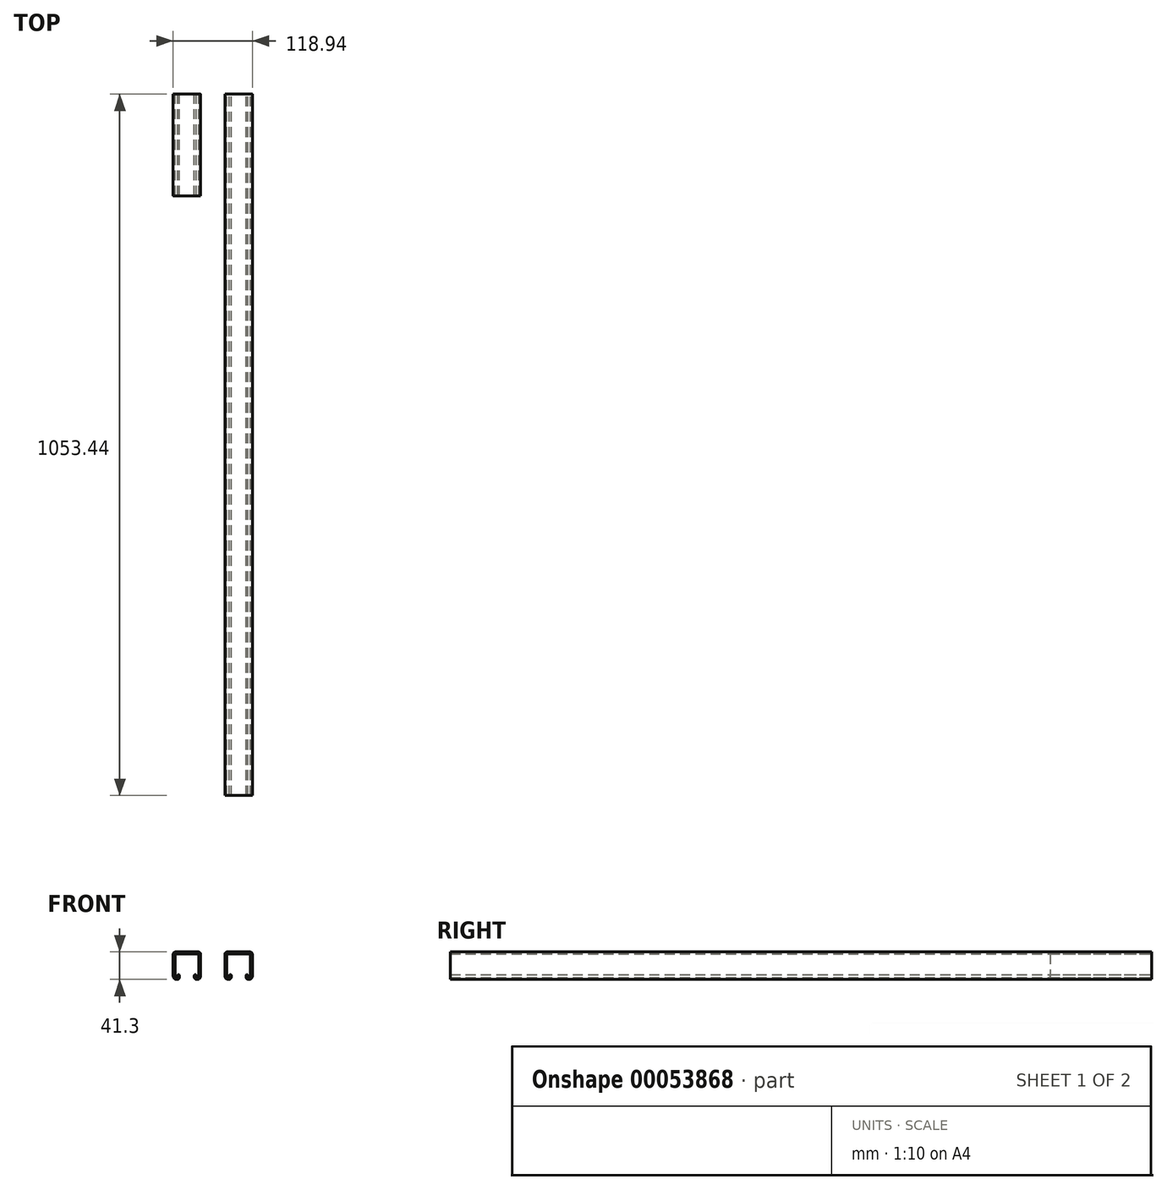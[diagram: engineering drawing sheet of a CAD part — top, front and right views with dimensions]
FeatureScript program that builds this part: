
annotation { "Feature Type Name" : "Feature", "Feature Type Description" : "" }
export const myFeature = defineFeature(function(context is Context, id is Id, definition is map)
    precondition{}
    {
        {
            var Q0;
            Q0=qCreatedBy(makeId("Front.planeOp"),FACE);
            var sketch = newSketch(context, id + "F0", { "sketchPlane" : qUnion([Q0])});
            skArc(sketch, "E0.0", {"start": v(5.05, 41.29) * mm, "mid": v(1.47, 39.8) * mm, "end": v(-0.01, 36.23) * mm});
            skFitSpline(sketch, "E0.1", {"points": [v(6.06, 41.29) * mm, v(5.73, 41.29) * mm, v(5.39, 41.29) * mm, v(5.05, 41.29) * mm]});
            skArc(sketch, "E0.2", {"start": v(9.54, 37.81) * mm, "mid": v(8.52, 40.27) * mm, "end": v(6.06, 41.29) * mm});
            skFitSpline(sketch, "E0.3", {"points": [v(9.54, 35.47) * mm, v(9.54, 36.25) * mm, v(9.54, 37.03) * mm, v(9.54, 37.81) * mm]});
            skArc(sketch, "E0.4", {"start": v(6.85, 35.47) * mm, "mid": v(8.2, 34.13) * mm, "end": v(9.54, 35.47) * mm});
            skFitSpline(sketch, "E0.5", {"points": [v(34.43, 35.47) * mm, v(34.43, 36.25) * mm, v(34.43, 37.03) * mm, v(34.43, 37.81) * mm]});
            skArc(sketch, "E0.6", {"start": v(31.74, 35.47) * mm, "mid": v(33.08, 34.13) * mm, "end": v(34.43, 35.47) * mm});
            skFitSpline(sketch, "E0.7", {"points": [v(31.74, 37.81) * mm, v(31.74, 37.03) * mm, v(31.74, 36.25) * mm, v(31.74, 35.47) * mm]});
            skArc(sketch, "E0.8", {"start": v(35.21, 41.29) * mm, "mid": v(32.75, 40.27) * mm, "end": v(31.74, 37.81) * mm});
            skFitSpline(sketch, "E0.9", {"points": [v(36.23, 41.29) * mm, v(35.89, 41.29) * mm, v(35.55, 41.29) * mm, v(35.21, 41.29) * mm]});
            skArc(sketch, "E0.10", {"start": v(41.29, 36.23) * mm, "mid": v(39.8, 39.8) * mm, "end": v(36.23, 41.29) * mm});
            skArc(sketch, "E0.11", {"start": v(-0.01, 3.46) * mm, "mid": v(1, 1) * mm, "end": v(3.46, -0.01) * mm});
            skFitSpline(sketch, "E0.12", {"points": [v(3.46, -0.01) * mm, v(14.91, -0.01) * mm, v(26.36, -0.01) * mm, v(37.81, -0.01) * mm]});
            skArc(sketch, "E0.13", {"start": v(37.81, -0.01) * mm, "mid": v(40.27, 1) * mm, "end": v(41.29, 3.46) * mm});
            skFitSpline(sketch, "E0.14", {"points": [v(41.29, 3.46) * mm, v(41.29, 14.38) * mm, v(41.29, 25.3) * mm, v(41.29, 36.23) * mm]});
            skArc(sketch, "E0.15", {"start": v(34.43, 37.81) * mm, "mid": v(34.66, 38.37) * mm, "end": v(35.21, 38.6) * mm});
            skFitSpline(sketch, "E0.16", {"points": [v(35.21, 38.6) * mm, v(35.55, 38.6) * mm, v(35.89, 38.6) * mm, v(36.23, 38.6) * mm]});
            skArc(sketch, "E0.17", {"start": v(36.23, 38.6) * mm, "mid": v(37.9, 37.9) * mm, "end": v(38.6, 36.23) * mm});
            skFitSpline(sketch, "E0.18", {"points": [v(38.6, 3.46) * mm, v(38.6, 14.38) * mm, v(38.6, 25.3) * mm, v(38.6, 36.23) * mm]});
            skArc(sketch, "E0.19", {"start": v(38.6, 3.46) * mm, "mid": v(38.37, 2.9) * mm, "end": v(37.81, 2.68) * mm});
            skFitSpline(sketch, "E0.20", {"points": [v(-0.01, 36.23) * mm, v(-0.01, 25.3) * mm, v(-0.01, 14.38) * mm, v(-0.01, 3.46) * mm]});
            skFitSpline(sketch, "E0.21", {"points": [v(37.81, 2.68) * mm, v(26.36, 2.68) * mm, v(14.91, 2.68) * mm, v(3.46, 2.68) * mm]});
            skArc(sketch, "E0.22", {"start": v(3.46, 2.68) * mm, "mid": v(2.9, 2.9) * mm, "end": v(2.68, 3.46) * mm});
            skFitSpline(sketch, "E0.23", {"points": [v(2.68, 3.46) * mm, v(2.68, 14.38) * mm, v(2.68, 25.3) * mm, v(2.68, 36.23) * mm]});
            skArc(sketch, "E0.24", {"start": v(2.68, 36.23) * mm, "mid": v(3.37, 37.9) * mm, "end": v(5.05, 38.6) * mm});
            skFitSpline(sketch, "E0.25", {"points": [v(5.05, 38.6) * mm, v(5.39, 38.6) * mm, v(5.73, 38.6) * mm, v(6.06, 38.6) * mm]});
            skArc(sketch, "E0.26", {"start": v(6.06, 38.6) * mm, "mid": v(6.62, 38.37) * mm, "end": v(6.85, 37.81) * mm});
            skFitSpline(sketch, "E0.27", {"points": [v(6.85, 37.81) * mm, v(6.85, 37.03) * mm, v(6.85, 36.25) * mm, v(6.85, 35.47) * mm]});
            skLineSegment(sketch, "E1", {"start": v(-9.67, -3.97) * mm, "end": v(55.26, -3.97) * mm});
            skFitSpline(sketch, "E2.MirrorCS", {"points": [v(-0.01, -44.16) * mm, v(-0.01, -33.24) * mm, v(-0.01, -22.32) * mm, v(-0.01, -11.4) * mm]});
            skFitSpline(sketch, "E3.MirrorCS", {"points": [v(2.68, -11.4) * mm, v(2.68, -22.32) * mm, v(2.68, -33.24) * mm, v(2.68, -44.16) * mm]});
            skArc(sketch, "E4.MirrorCS", {"start": v(5.05, -49.22) * mm, "mid": v(1.47, -47.74) * mm, "end": v(-0.01, -44.16) * mm});
            skArc(sketch, "E5.MirrorCS", {"start": v(9.54, -45.75) * mm, "mid": v(8.52, -48.2) * mm, "end": v(6.06, -49.22) * mm});
            skFitSpline(sketch, "E6.MirrorCS", {"points": [v(9.54, -43.4) * mm, v(9.54, -44.19) * mm, v(9.54, -44.97) * mm, v(9.54, -45.75) * mm]});
            skArc(sketch, "E7.MirrorCS", {"start": v(6.85, -43.4) * mm, "mid": v(8.2, -42.06) * mm, "end": v(9.54, -43.4) * mm});
            skFitSpline(sketch, "E8.MirrorCS", {"points": [v(6.85, -45.75) * mm, v(6.85, -44.97) * mm, v(6.85, -44.19) * mm, v(6.85, -43.4) * mm]});
            skArc(sketch, "E9.MirrorCS", {"start": v(6.06, -46.53) * mm, "mid": v(6.62, -46.3) * mm, "end": v(6.85, -45.75) * mm});
            skFitSpline(sketch, "E10.MirrorCS", {"points": [v(5.05, -46.53) * mm, v(5.39, -46.53) * mm, v(5.73, -46.53) * mm, v(6.06, -46.53) * mm]});
            skArc(sketch, "E11.MirrorCS", {"start": v(2.68, -44.16) * mm, "mid": v(3.37, -45.84) * mm, "end": v(5.05, -46.53) * mm});
            skFitSpline(sketch, "E12.MirrorCS", {"points": [v(6.06, -49.22) * mm, v(5.73, -49.22) * mm, v(5.39, -49.22) * mm, v(5.05, -49.22) * mm]});
            skArc(sketch, "E13.MirrorCS", {"start": v(3.46, -10.61) * mm, "mid": v(2.9, -10.84) * mm, "end": v(2.68, -11.4) * mm});
            skArc(sketch, "E14.MirrorCS", {"start": v(-0.01, -11.4) * mm, "mid": v(1, -8.94) * mm, "end": v(3.46, -7.92) * mm});
            skFitSpline(sketch, "E15.MirrorCS", {"points": [v(3.46, -7.92) * mm, v(14.91, -7.92) * mm, v(26.36, -7.92) * mm, v(37.81, -7.92) * mm]});
            skFitSpline(sketch, "E16.MirrorCS", {"points": [v(37.81, -10.61) * mm, v(26.36, -10.61) * mm, v(14.91, -10.61) * mm, v(3.46, -10.61) * mm]});
            skArc(sketch, "E17.MirrorCS", {"start": v(37.81, -7.92) * mm, "mid": v(40.27, -8.94) * mm, "end": v(41.29, -11.4) * mm});
            skFitSpline(sketch, "E18.MirrorCS", {"points": [v(38.6, -11.4) * mm, v(38.6, -22.32) * mm, v(38.6, -33.24) * mm, v(38.6, -44.16) * mm]});
            skFitSpline(sketch, "E19.MirrorCS", {"points": [v(41.29, -11.4) * mm, v(41.29, -22.32) * mm, v(41.29, -33.24) * mm, v(41.29, -44.16) * mm]});
            skArc(sketch, "E20.MirrorCS", {"start": v(38.6, -11.4) * mm, "mid": v(38.37, -10.84) * mm, "end": v(37.81, -10.61) * mm});
            skArc(sketch, "E21.MirrorCS", {"start": v(31.74, -43.4) * mm, "mid": v(33.08, -42.06) * mm, "end": v(34.43, -43.4) * mm});
            skFitSpline(sketch, "E22.MirrorCS", {"points": [v(31.74, -45.75) * mm, v(31.74, -44.97) * mm, v(31.74, -44.19) * mm, v(31.74, -43.4) * mm]});
            skArc(sketch, "E23.MirrorCS", {"start": v(35.21, -49.22) * mm, "mid": v(32.75, -48.2) * mm, "end": v(31.74, -45.75) * mm});
            skFitSpline(sketch, "E24.MirrorCS", {"points": [v(36.23, -49.22) * mm, v(35.89, -49.22) * mm, v(35.55, -49.22) * mm, v(35.21, -49.22) * mm]});
            skArc(sketch, "E25.MirrorCS", {"start": v(34.43, -45.75) * mm, "mid": v(34.66, -46.3) * mm, "end": v(35.21, -46.53) * mm});
            skFitSpline(sketch, "E26.MirrorCS", {"points": [v(34.43, -43.4) * mm, v(34.43, -44.19) * mm, v(34.43, -44.97) * mm, v(34.43, -45.75) * mm]});
            skFitSpline(sketch, "E27.MirrorCS", {"points": [v(35.21, -46.53) * mm, v(35.55, -46.53) * mm, v(35.89, -46.53) * mm, v(36.23, -46.53) * mm]});
            skArc(sketch, "E28.MirrorCS", {"start": v(36.23, -46.53) * mm, "mid": v(37.9, -45.84) * mm, "end": v(38.6, -44.16) * mm});
            skArc(sketch, "E29.MirrorCS", {"start": v(41.29, -44.16) * mm, "mid": v(39.8, -47.74) * mm, "end": v(36.23, -49.22) * mm});
            skLineSegment(sketch, "E30", {"start": v(63.23, 49.88) * mm, "end": v(63.23, -3.52) * mm});
            skFitSpline(sketch, "E31.MirrorCS", {"points": [v(85.18, 3.46) * mm, v(85.18, 14.38) * mm, v(85.18, 25.3) * mm, v(85.18, 36.23) * mm]});
            skFitSpline(sketch, "E32.MirrorCS", {"points": [v(87.87, 3.46) * mm, v(87.87, 14.38) * mm, v(87.87, 25.3) * mm, v(87.87, 36.23) * mm]});
            skFitSpline(sketch, "E33.MirrorCS", {"points": [v(123.79, 3.46) * mm, v(123.79, 14.38) * mm, v(123.79, 25.3) * mm, v(123.79, 36.23) * mm]});
            skFitSpline(sketch, "E34.MirrorCS", {"points": [v(126.48, 36.23) * mm, v(126.48, 25.3) * mm, v(126.48, 14.38) * mm, v(126.48, 3.46) * mm]});
            skArc(sketch, "E35.MirrorCS", {"start": v(126.48, 3.46) * mm, "mid": v(125.46, 1) * mm, "end": v(123, -0.01) * mm});
            skFitSpline(sketch, "E36.MirrorCS", {"points": [v(88.65, 2.68) * mm, v(100.1, 2.68) * mm, v(111.56, 2.68) * mm, v(123, 2.68) * mm]});
            skFitSpline(sketch, "E37.MirrorCS", {"points": [v(123, -0.01) * mm, v(111.56, -0.01) * mm, v(100.1, -0.01) * mm, v(88.65, -0.01) * mm]});
            skArc(sketch, "E38.MirrorCS", {"start": v(88.65, -0.01) * mm, "mid": v(86.2, 1) * mm, "end": v(85.18, 3.46) * mm});
            skFitSpline(sketch, "E39.MirrorCS", {"points": [v(85.18, 3.46) * mm, v(85.18, 14.38) * mm, v(85.18, 25.3) * mm, v(85.18, 36.23) * mm]});
            skArc(sketch, "E40.MirrorCS", {"start": v(90.24, 38.6) * mm, "mid": v(88.57, 37.9) * mm, "end": v(87.87, 36.23) * mm});
            skArc(sketch, "E41.MirrorCS", {"start": v(85.18, 36.23) * mm, "mid": v(86.66, 39.8) * mm, "end": v(90.24, 41.29) * mm});
            skFitSpline(sketch, "E42.MirrorCS", {"points": [v(90.24, 41.29) * mm, v(90.58, 41.29) * mm, v(90.92, 41.29) * mm, v(91.26, 41.29) * mm]});
            skArc(sketch, "E43.MirrorCS", {"start": v(91.26, 41.29) * mm, "mid": v(93.71, 40.27) * mm, "end": v(94.73, 37.81) * mm});
            skFitSpline(sketch, "E44.MirrorCS", {"points": [v(94.73, 37.81) * mm, v(94.73, 37.03) * mm, v(94.73, 36.25) * mm, v(94.73, 35.47) * mm]});
            skArc(sketch, "E45.MirrorCS", {"start": v(94.73, 35.47) * mm, "mid": v(93.39, 34.13) * mm, "end": v(92.04, 35.47) * mm});
            skFitSpline(sketch, "E46.MirrorCS", {"points": [v(92.04, 35.47) * mm, v(92.04, 36.25) * mm, v(92.04, 37.03) * mm, v(92.04, 37.81) * mm]});
            skArc(sketch, "E47.MirrorCS", {"start": v(92.04, 37.81) * mm, "mid": v(91.81, 38.37) * mm, "end": v(91.26, 38.6) * mm});
            skArc(sketch, "E48.MirrorCS", {"start": v(121.42, 41.29) * mm, "mid": v(125, 39.8) * mm, "end": v(126.48, 36.23) * mm});
            skFitSpline(sketch, "E49.MirrorCS", {"points": [v(120.4, 41.29) * mm, v(120.74, 41.29) * mm, v(121.08, 41.29) * mm, v(121.42, 41.29) * mm]});
            skArc(sketch, "E50.MirrorCS", {"start": v(123.79, 36.23) * mm, "mid": v(123.1, 37.9) * mm, "end": v(121.42, 38.6) * mm});
            skArc(sketch, "E51.MirrorCS", {"start": v(120.4, 38.6) * mm, "mid": v(119.85, 38.37) * mm, "end": v(119.62, 37.81) * mm});
            skFitSpline(sketch, "E52.MirrorCS", {"points": [v(119.62, 37.81) * mm, v(119.62, 37.03) * mm, v(119.62, 36.25) * mm, v(119.62, 35.47) * mm]});
            skArc(sketch, "E53.MirrorCS", {"start": v(119.62, 35.47) * mm, "mid": v(118.28, 34.13) * mm, "end": v(116.93, 35.47) * mm});
            skFitSpline(sketch, "E54.MirrorCS", {"points": [v(116.93, 35.47) * mm, v(116.93, 36.25) * mm, v(116.93, 37.03) * mm, v(116.93, 37.81) * mm]});
            skArc(sketch, "E55.MirrorCS", {"start": v(116.93, 37.81) * mm, "mid": v(117.95, 40.27) * mm, "end": v(120.4, 41.29) * mm});
            skArc(sketch, "E56.MirrorCS", {"start": v(87.87, 3.46) * mm, "mid": v(88.1, 2.9) * mm, "end": v(88.65, 2.68) * mm});
            skArc(sketch, "E57.MirrorCS", {"start": v(123, 2.68) * mm, "mid": v(123.56, 2.9) * mm, "end": v(123.79, 3.46) * mm});
            skFitSpline(sketch, "E58.MirrorCS", {"points": [v(91.26, 38.6) * mm, v(90.92, 38.6) * mm, v(90.58, 38.6) * mm, v(90.24, 38.6) * mm]});
            skFitSpline(sketch, "E59.MirrorCS", {"points": [v(121.42, 38.6) * mm, v(121.08, 38.6) * mm, v(120.74, 38.6) * mm, v(120.4, 38.6) * mm]});
            skArc(sketch, "E60.MirrorCS", {"start": v(88.65, 0.2) * mm, "mid": v(86.2, -0.8) * mm, "end": v(85.17, -3.26) * mm});
            skFitSpline(sketch, "E61.MirrorCS", {"points": [v(85.17, -3.26) * mm, v(85.12, -14.18) * mm, v(85.07, -25.1) * mm, v(85.02, -36.03) * mm]});
            skFitSpline(sketch, "E62.MirrorCS", {"points": [v(87.86, -3.27) * mm, v(87.8, -14.2) * mm, v(87.76, -25.12) * mm, v(87.7, -36.04) * mm]});
            skArc(sketch, "E63.MirrorCS", {"start": v(87.86, -3.27) * mm, "mid": v(88.09, -2.72) * mm, "end": v(88.64, -2.5) * mm});
            skFitSpline(sketch, "E64.MirrorCS", {"points": [v(88.64, -2.5) * mm, v(100.1, -2.55) * mm, v(111.54, -2.6) * mm, v(123, -2.65) * mm]});
            skArc(sketch, "E65.MirrorCS", {"start": v(123, -2.65) * mm, "mid": v(123.55, -2.88) * mm, "end": v(123.77, -3.43) * mm});
            skArc(sketch, "E66.MirrorCS", {"start": v(126.47, -3.45) * mm, "mid": v(125.46, -0.99) * mm, "end": v(123, 0.04) * mm});
            skFitSpline(sketch, "E67.MirrorCS", {"points": [v(126.32, -36.21) * mm, v(126.37, -25.3) * mm, v(126.42, -14.37) * mm, v(126.47, -3.45) * mm]});
            skFitSpline(sketch, "E68.MirrorCS", {"points": [v(123.77, -3.43) * mm, v(123.72, -14.36) * mm, v(123.68, -25.28) * mm, v(123.63, -36.2) * mm]});
            skArc(sketch, "E69.MirrorCS", {"start": v(85.02, -36.03) * mm, "mid": v(86.48, -39.61) * mm, "end": v(90.06, -41.1) * mm});
            skArc(sketch, "E70.MirrorCS", {"start": v(90.07, -38.42) * mm, "mid": v(88.4, -37.72) * mm, "end": v(87.7, -36.04) * mm});
            skFitSpline(sketch, "E71.MirrorCS", {"points": [v(90.06, -41.1) * mm, v(90.4, -41.11) * mm, v(90.73, -41.11) * mm, v(91.07, -41.11) * mm]});
            skFitSpline(sketch, "E72.MirrorCS", {"points": [v(91.08, -38.42) * mm, v(90.75, -38.42) * mm, v(90.4, -38.42) * mm, v(90.07, -38.42) * mm]});
            skArc(sketch, "E73.MirrorCS", {"start": v(91.87, -37.64) * mm, "mid": v(91.64, -38.2) * mm, "end": v(91.08, -38.42) * mm});
            skArc(sketch, "E74.MirrorCS", {"start": v(91.07, -41.11) * mm, "mid": v(93.53, -40.1) * mm, "end": v(94.56, -37.66) * mm});
            skFitSpline(sketch, "E75.MirrorCS", {"points": [v(94.56, -37.66) * mm, v(94.56, -36.88) * mm, v(94.57, -36.1) * mm, v(94.57, -35.31) * mm]});
            skArc(sketch, "E76.MirrorCS", {"start": v(94.57, -35.31) * mm, "mid": v(93.23, -33.96) * mm, "end": v(91.88, -35.3) * mm});
            skFitSpline(sketch, "E77.MirrorCS", {"points": [v(91.88, -35.3) * mm, v(91.88, -36.08) * mm, v(91.87, -36.86) * mm, v(91.87, -37.64) * mm]});
            skFitSpline(sketch, "E78.MirrorCS", {"points": [v(119.45, -37.77) * mm, v(119.46, -36.99) * mm, v(119.46, -36.2) * mm, v(119.46, -35.43) * mm]});
            skArc(sketch, "E79.MirrorCS", {"start": v(120.23, -38.55) * mm, "mid": v(119.68, -38.32) * mm, "end": v(119.45, -37.77) * mm});
            skFitSpline(sketch, "E80.MirrorCS", {"points": [v(121.25, -38.56) * mm, v(120.9, -38.56) * mm, v(120.57, -38.56) * mm, v(120.23, -38.55) * mm]});
            skArc(sketch, "E81.MirrorCS", {"start": v(123.63, -36.2) * mm, "mid": v(122.92, -37.87) * mm, "end": v(121.25, -38.56) * mm});
            skFitSpline(sketch, "E82.MirrorCS", {"points": [v(119.45, -37.77) * mm, v(119.46, -36.99) * mm, v(119.46, -36.2) * mm, v(119.46, -35.43) * mm]});
            skArc(sketch, "E83.MirrorCS", {"start": v(119.46, -35.43) * mm, "mid": v(118.12, -34.07) * mm, "end": v(116.77, -35.41) * mm});
            skFitSpline(sketch, "E84.MirrorCS", {"points": [v(116.77, -35.41) * mm, v(116.77, -36.2) * mm, v(116.76, -36.98) * mm, v(116.76, -37.76) * mm]});
            skArc(sketch, "E85.MirrorCS", {"start": v(116.76, -37.76) * mm, "mid": v(117.77, -40.22) * mm, "end": v(120.22, -41.25) * mm});
            skFitSpline(sketch, "E86.MirrorCS", {"points": [v(120.22, -41.25) * mm, v(120.56, -41.25) * mm, v(120.9, -41.25) * mm, v(121.23, -41.25) * mm]});
            skArc(sketch, "E87.MirrorCS", {"start": v(121.23, -41.25) * mm, "mid": v(124.82, -39.78) * mm, "end": v(126.32, -36.21) * mm});
            skFitSpline(sketch, "E88.MirrorCS", {"points": [v(126.32, -36.21) * mm, v(126.37, -25.3) * mm, v(126.42, -14.37) * mm, v(126.47, -3.45) * mm]});
            skLineSegment(sketch, "E89", {"start": v(-18.18, 60.45) * mm, "end": v(-18.18, -59.78) * mm});
            skFitSpline(sketch, "E90.MirrorCS", {"points": [v(-36.35, -44.16) * mm, v(-36.35, -33.24) * mm, v(-36.35, -22.32) * mm, v(-36.35, -11.4) * mm]});
            skFitSpline(sketch, "E91.MirrorCS", {"points": [v(-39.05, -11.4) * mm, v(-39.05, -22.32) * mm, v(-39.05, -33.24) * mm, v(-39.05, -44.16) * mm]});
            skArc(sketch, "E92.MirrorCS", {"start": v(-36.35, -11.4) * mm, "mid": v(-37.37, -8.94) * mm, "end": v(-39.83, -7.92) * mm});
            skArc(sketch, "E93.MirrorCS", {"start": v(-39.83, -10.61) * mm, "mid": v(-39.27, -10.84) * mm, "end": v(-39.05, -11.4) * mm});
            skFitSpline(sketch, "E94.MirrorCS", {"points": [v(-39.83, -7.92) * mm, v(-51.28, -7.92) * mm, v(-62.73, -7.92) * mm, v(-74.18, -7.92) * mm]});
            skFitSpline(sketch, "E95.MirrorCS", {"points": [v(-74.18, -10.61) * mm, v(-62.73, -10.61) * mm, v(-51.28, -10.61) * mm, v(-39.83, -10.61) * mm]});
            skArc(sketch, "E96.MirrorCS", {"start": v(-74.18, -7.92) * mm, "mid": v(-76.64, -8.94) * mm, "end": v(-77.65, -11.4) * mm});
            skFitSpline(sketch, "E97.MirrorCS", {"points": [v(-77.65, -11.4) * mm, v(-77.65, -22.32) * mm, v(-77.65, -33.24) * mm, v(-77.65, -44.16) * mm]});
            skArc(sketch, "E98.MirrorCS", {"start": v(-74.96, -11.4) * mm, "mid": v(-74.73, -10.84) * mm, "end": v(-74.18, -10.61) * mm});
            skFitSpline(sketch, "E99.MirrorCS", {"points": [v(-74.96, -11.4) * mm, v(-74.96, -22.32) * mm, v(-74.96, -33.24) * mm, v(-74.96, -44.16) * mm]});
            skArc(sketch, "E100.MirrorCS", {"start": v(-72.6, -46.53) * mm, "mid": v(-74.27, -45.84) * mm, "end": v(-74.96, -44.16) * mm});
            skArc(sketch, "E101.MirrorCS", {"start": v(-77.65, -44.16) * mm, "mid": v(-76.17, -47.74) * mm, "end": v(-72.6, -49.22) * mm});
            skFitSpline(sketch, "E102.MirrorCS", {"points": [v(-72.6, -49.22) * mm, v(-72.25, -49.22) * mm, v(-71.92, -49.22) * mm, v(-71.58, -49.22) * mm]});
            skFitSpline(sketch, "E103.MirrorCS", {"points": [v(-71.58, -46.53) * mm, v(-71.92, -46.53) * mm, v(-72.25, -46.53) * mm, v(-72.6, -46.53) * mm]});
            skArc(sketch, "E104.MirrorCS", {"start": v(-70.8, -45.75) * mm, "mid": v(-71.02, -46.3) * mm, "end": v(-71.58, -46.53) * mm});
            skFitSpline(sketch, "E105.MirrorCS", {"points": [v(-70.8, -43.4) * mm, v(-70.8, -44.19) * mm, v(-70.8, -44.97) * mm, v(-70.8, -45.75) * mm]});
            skArc(sketch, "E106.MirrorCS", {"start": v(-68.1, -43.4) * mm, "mid": v(-69.45, -42.06) * mm, "end": v(-70.8, -43.4) * mm});
            skFitSpline(sketch, "E107.MirrorCS", {"points": [v(-68.1, -45.75) * mm, v(-68.1, -44.97) * mm, v(-68.1, -44.19) * mm, v(-68.1, -43.4) * mm]});
            skArc(sketch, "E108.MirrorCS", {"start": v(-71.58, -49.22) * mm, "mid": v(-69.12, -48.2) * mm, "end": v(-68.1, -45.75) * mm});
            skFitSpline(sketch, "E109.MirrorCS", {"points": [v(-45.9, -43.4) * mm, v(-45.9, -44.19) * mm, v(-45.9, -44.97) * mm, v(-45.9, -45.75) * mm]});
            skArc(sketch, "E110.MirrorCS", {"start": v(-43.21, -43.4) * mm, "mid": v(-44.56, -42.06) * mm, "end": v(-45.9, -43.4) * mm});
            skFitSpline(sketch, "E111.MirrorCS", {"points": [v(-43.21, -45.75) * mm, v(-43.21, -44.97) * mm, v(-43.21, -44.19) * mm, v(-43.21, -43.4) * mm]});
            skArc(sketch, "E112.MirrorCS", {"start": v(-45.9, -45.75) * mm, "mid": v(-44.89, -48.2) * mm, "end": v(-42.43, -49.22) * mm});
            skArc(sketch, "E113.MirrorCS", {"start": v(-42.43, -46.53) * mm, "mid": v(-42.98, -46.3) * mm, "end": v(-43.21, -45.75) * mm});
            skFitSpline(sketch, "E114.MirrorCS", {"points": [v(-41.41, -46.53) * mm, v(-41.75, -46.53) * mm, v(-42.1, -46.53) * mm, v(-42.43, -46.53) * mm]});
            skFitSpline(sketch, "E115.MirrorCS", {"points": [v(-42.43, -49.22) * mm, v(-42.1, -49.22) * mm, v(-41.75, -49.22) * mm, v(-41.41, -49.22) * mm]});
            skArc(sketch, "E116.MirrorCS", {"start": v(-41.41, -49.22) * mm, "mid": v(-37.84, -47.74) * mm, "end": v(-36.35, -44.16) * mm});
            skArc(sketch, "E117.MirrorCS", {"start": v(-39.05, -44.16) * mm, "mid": v(-39.74, -45.84) * mm, "end": v(-41.41, -46.53) * mm});
            skSolve(sketch);
        }
        {
            var Q0;
            Q0=makeQuery(id+"F0.imprint","IMPRINT",FACE,{"disambiguationData":[TD([[makeQuery(id+"F0.imprint","IMPRINT",EDGE,{"derivedFrom":sQuery(id+"F0.wireOp",EDGE,"E2.MirrorCS")}),-1.0]])]});
            extrude(context, id + "F1", {"entities" : qUnion([Q0]), "depth" : 1053.44 * mm});
        }
        {
            var Q0;
            Q0=makeQuery(id+"F0.imprint","IMPRINT",FACE,{"disambiguationData":[TD([[makeQuery(id+"F0.imprint","IMPRINT",EDGE,{"derivedFrom":sQuery(id+"F0.wireOp",EDGE,"E90.MirrorCS")}),1.0]])]});
            extrude(context, id + "F2", {"entities" : qUnion([Q0]), "depth" : 152.57 * mm});
        }
    });
